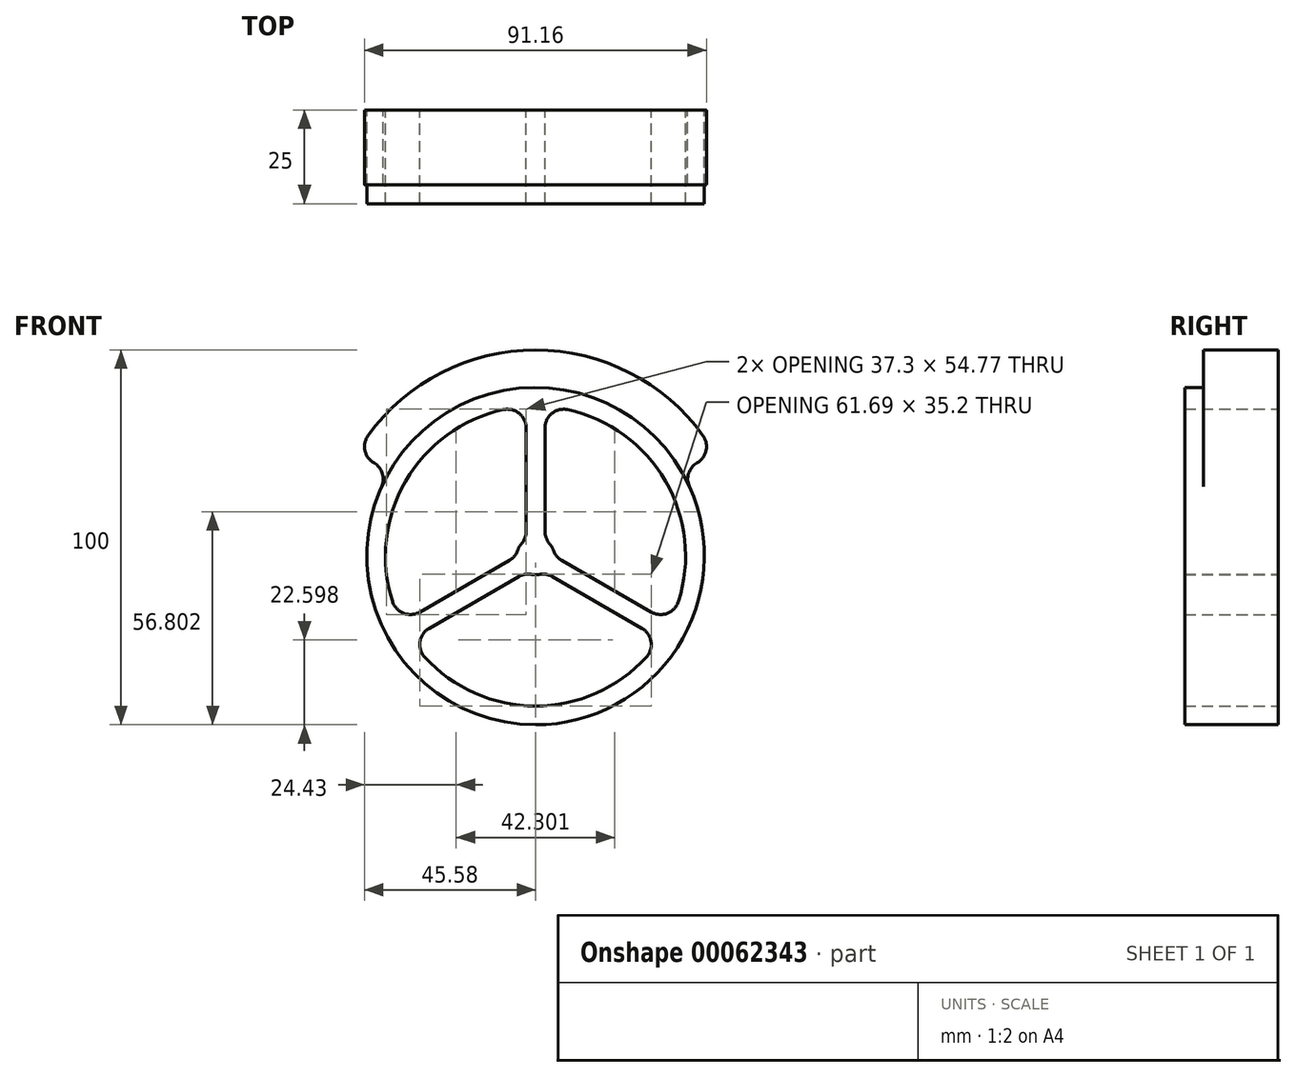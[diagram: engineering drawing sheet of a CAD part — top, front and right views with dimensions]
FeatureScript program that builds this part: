
annotation { "Feature Type Name" : "Feature", "Feature Type Description" : "" }
export const myFeature = defineFeature(function(context is Context, id is Id, definition is map)
    precondition{}
    {
        {
            var Q0;
            Q0=qCreatedBy(makeId("Front.planeOp"),FACE);
            var sketch = newSketch(context, id + "F0", { "sketchPlane" : qUnion([Q0])});
            skArc(sketch, "E0", {"start": v(-8.57, 39.07) * mm, "mid": v(-34.64, 20) * mm, "end": v(-38.12, -12.11) * mm});
            skArc(sketch, "E1", {"start": v(-41.03, 18.5) * mm, "mid": v(0, -45) * mm, "end": v(41.03, 18.5) * mm});
            skLineSegment(sketch, "E2", {"start": v(-2.5, 6.61) * mm, "end": v(-2.5, 34.19) * mm});
            skArc(sketch, "E3", {"start": v(-0.99, -4.9) * mm, "mid": v(0, -5) * mm, "end": v(0.99, -4.9) * mm});
            skLineSegment(sketch, "E4.trimOffspring", {"start": v(4.48, -5.47) * mm, "end": v(28.36, -19.26) * mm});
            skLineSegment(sketch, "E5.trimOffspring", {"start": v(-4.48, -5.47) * mm, "end": v(-28.36, -19.26) * mm});
            skLineSegment(sketch, "E6.trimOffspring", {"start": v(-6.98, -1.14) * mm, "end": v(-30.86, -14.93) * mm});
            skLineSegment(sketch, "E7.trimOffspring", {"start": v(2.5, 6.61) * mm, "end": v(2.5, 34.19) * mm});
            skLineSegment(sketch, "E8.trimOffspring", {"start": v(6.98, -1.14) * mm, "end": v(30.86, -14.93) * mm});
            skArc(sketch, "E9.trimOffspring", {"start": v(4.74, 1.6) * mm, "mid": v(4.33, 2.5) * mm, "end": v(3.75, 3.3) * mm});
            skArc(sketch, "E10.trimOffspring", {"start": v(-3.75, 3.3) * mm, "mid": v(-4.33, 2.5) * mm, "end": v(-4.74, 1.6) * mm});
            skPoint(sketch, "E11.visualSharp", {"position": v(-2.5, -4.33) * mm});
            skArc(sketch, "E11.filletArc", {"start": v(-0.99, -4.9) * mm, "mid": v(-2.79, -4.87) * mm, "end": v(-4.48, -5.47) * mm});
            skPoint(sketch, "E12.visualSharp", {"position": v(2.5, -4.33) * mm});
            skArc(sketch, "E12.filletArc", {"start": v(4.48, -5.47) * mm, "mid": v(2.79, -4.87) * mm, "end": v(0.99, -4.9) * mm});
            skPoint(sketch, "E13.visualSharp", {"position": v(5, 0) * mm});
            skArc(sketch, "E13.filletArc", {"start": v(4.74, 1.6) * mm, "mid": v(5.6, 0.02) * mm, "end": v(6.98, -1.14) * mm});
            skPoint(sketch, "E14.visualSharp", {"position": v(2.5, 4.33) * mm});
            skArc(sketch, "E14.filletArc", {"start": v(2.5, 6.61) * mm, "mid": v(2.82, 4.85) * mm, "end": v(3.75, 3.3) * mm});
            skPoint(sketch, "E15.visualSharp", {"position": v(-2.5, 4.33) * mm});
            skArc(sketch, "E15.filletArc", {"start": v(-3.75, 3.3) * mm, "mid": v(-2.82, 4.85) * mm, "end": v(-2.5, 6.61) * mm});
            skPoint(sketch, "E16.visualSharp", {"position": v(-5, 0) * mm});
            skArc(sketch, "E16.filletArc", {"start": v(-6.98, -1.14) * mm, "mid": v(-5.6, 0.02) * mm, "end": v(-4.74, 1.6) * mm});
            skPoint(sketch, "E17.visualSharp", {"position": v(2.5, 39.92) * mm});
            skArc(sketch, "E17.filletArc", {"start": v(8.57, 39.07) * mm, "mid": v(4.37, 38.08) * mm, "end": v(2.5, 34.19) * mm});
            skPoint(sketch, "E18.visualSharp", {"position": v(-2.5, 39.92) * mm});
            skArc(sketch, "E18.filletArc", {"start": v(-2.5, 34.19) * mm, "mid": v(-4.37, 38.08) * mm, "end": v(-8.57, 39.07) * mm});
            skArc(sketch, "E19.trimOffspring", {"start": v(-29.55, -26.96) * mm, "mid": v(0, -40) * mm, "end": v(29.55, -26.96) * mm});
            skArc(sketch, "E20.trimOffspring", {"start": v(38.12, -12.11) * mm, "mid": v(34.64, 20) * mm, "end": v(8.57, 39.07) * mm});
            skPoint(sketch, "E21.visualSharp", {"position": v(-33.32, -22.13) * mm});
            skArc(sketch, "E21.filletArc", {"start": v(-28.36, -19.26) * mm, "mid": v(-30.8, -22.82) * mm, "end": v(-29.55, -26.96) * mm});
            skPoint(sketch, "E22.visualSharp", {"position": v(-35.82, -17.8) * mm});
            skArc(sketch, "E22.filletArc", {"start": v(-38.12, -12.11) * mm, "mid": v(-35.16, -15.26) * mm, "end": v(-30.86, -14.93) * mm});
            skPoint(sketch, "E23.visualSharp", {"position": v(33.32, -22.13) * mm});
            skArc(sketch, "E23.filletArc", {"start": v(29.55, -26.96) * mm, "mid": v(30.8, -22.82) * mm, "end": v(28.36, -19.26) * mm});
            skPoint(sketch, "E24.visualSharp", {"position": v(35.82, -17.8) * mm});
            skArc(sketch, "E24.filletArc", {"start": v(30.86, -14.93) * mm, "mid": v(35.16, -15.26) * mm, "end": v(38.12, -12.11) * mm});
            skArc(sketch, "E25", {"start": v(44.64, 32.13) * mm, "mid": v(0, 55) * mm, "end": v(-44.64, 32.13) * mm});
            skLineSegment(sketch, "E26.trimOffspring", {"start": v(-43.08, 24.87) * mm, "end": v(-43.08, 24.87) * mm});
            skLineSegment(sketch, "E27.trimOffspring", {"start": v(43.08, 24.87) * mm, "end": v(43.08, 24.87) * mm});
            skPoint(sketch, "E28.visualSharp", {"position": v(-47.63, 27.5) * mm});
            skArc(sketch, "E28.filletArc", {"start": v(-44.64, 32.13) * mm, "mid": v(-45.47, 28.15) * mm, "end": v(-43.08, 24.87) * mm});
            skPoint(sketch, "E29.visualSharp", {"position": v(-38.97, 22.5) * mm});
            skArc(sketch, "E29.filletArc", {"start": v(-41.03, 18.5) * mm, "mid": v(-40.83, 22.08) * mm, "end": v(-43.08, 24.87) * mm});
            skPoint(sketch, "E30.visualSharp", {"position": v(38.97, 22.5) * mm});
            skArc(sketch, "E30.filletArc", {"start": v(43.08, 24.87) * mm, "mid": v(40.83, 22.08) * mm, "end": v(41.03, 18.5) * mm});
            skPoint(sketch, "E31.visualSharp", {"position": v(47.63, 27.5) * mm});
            skArc(sketch, "E31.filletArc", {"start": v(43.08, 24.87) * mm, "mid": v(45.47, 28.15) * mm, "end": v(44.64, 32.13) * mm});
            skSolve(sketch);
        }
        {
            var Q0;
            Q0=makeQuery(id+"F0.imprint","IMPRINT",FACE,{"disambiguationData":[TD([[makeQuery(id+"F0.imprint","IMPRINT",EDGE,{"derivedFrom":sQuery(id+"F0.wireOp",EDGE,"E0")}),-1.0]])]});
            var Q1;
            Q1=makeQuery(id+"F0.imprint","IMPRINT",FACE,{"disambiguationData":[TD([[makeQuery(id+"F0.imprint","IMPRINT",EDGE,{"derivedFrom":sQuery(id+"F0.wireOp",EDGE,"E0")}),-1.0]])]});
            extrude(context, id + "F1", {"entities" : qUnion([Q0, Q1]), "depth" : 25 * mm});
        }
        {
            var Q0;
            Q0=makeQuery(id+"F1.opExtrude","CAP_FACE",FACE,{"disambiguationData":[OSD([sQuery(id+"F0.wireOp",EDGE,"E0"),sQuery(id+"F0.wireOp",EDGE,"E1"),sQuery(id+"F0.wireOp",EDGE,"E2"),sQuery(id+"F0.wireOp",EDGE,"E3"),sQuery(id+"F0.wireOp",EDGE,"E4.trimOffspring"),sQuery(id+"F0.wireOp",EDGE,"E5.trimOffspring"),sQuery(id+"F0.wireOp",EDGE,"E6.trimOffspring"),sQuery(id+"F0.wireOp",EDGE,"E7.trimOffspring"),sQuery(id+"F0.wireOp",EDGE,"E8.trimOffspring"),sQuery(id+"F0.wireOp",EDGE,"E9.trimOffspring"),sQuery(id+"F0.wireOp",EDGE,"E10.trimOffspring"),sQuery(id+"F0.wireOp",EDGE,"E11.filletArc"),sQuery(id+"F0.wireOp",EDGE,"E12.filletArc"),sQuery(id+"F0.wireOp",EDGE,"E13.filletArc"),sQuery(id+"F0.wireOp",EDGE,"E14.filletArc"),sQuery(id+"F0.wireOp",EDGE,"E15.filletArc"),sQuery(id+"F0.wireOp",EDGE,"E16.filletArc"),sQuery(id+"F0.wireOp",EDGE,"E17.filletArc"),sQuery(id+"F0.wireOp",EDGE,"E18.filletArc"),sQuery(id+"F0.wireOp",EDGE,"E19.trimOffspring"),sQuery(id+"F0.wireOp",EDGE,"E20.trimOffspring"),sQuery(id+"F0.wireOp",EDGE,"E21.filletArc"),sQuery(id+"F0.wireOp",EDGE,"E22.filletArc"),sQuery(id+"F0.wireOp",EDGE,"E23.filletArc"),sQuery(id+"F0.wireOp",EDGE,"E24.filletArc"),sQuery(id+"F0.wireOp",EDGE,"E25"),sQuery(id+"F0.wireOp",EDGE,"E28.filletArc"),sQuery(id+"F0.wireOp",EDGE,"E29.filletArc"),sQuery(id+"F0.wireOp",EDGE,"E30.filletArc"),sQuery(id+"F0.wireOp",EDGE,"E31.filletArc")])],"isStart":false});
            var sketch = newSketch(context, id + "F2", { "sketchPlane" : qUnion([Q0])});
            skCircle(sketch, "E32", {"center": v(0, 0) * mm, "radius": 45 * mm});
            skSolve(sketch);
        }
        {
            var Q0;
            Q0=makeQuery(id+"F2.imprint","IMPRINT",FACE,{"disambiguationData":[TD([[makeQuery(id+"F2.imprint","IMPRINT",EDGE,{"derivedFrom":makeQuery(id+"F1.opExtrude","CAP_EDGE",EDGE,{"disambiguationData":[OSD([sQuery(id+"F0.wireOp",EDGE,"E25")])],"isStart":false})}),1.0]])]});
            extrude(context, id + "F3", {"entities" : qUnion([Q0]), "operationType" : NewBodyOperationType.REMOVE, "oppositeDirection" : true, "depth" : 5 * mm});
        }
    });
